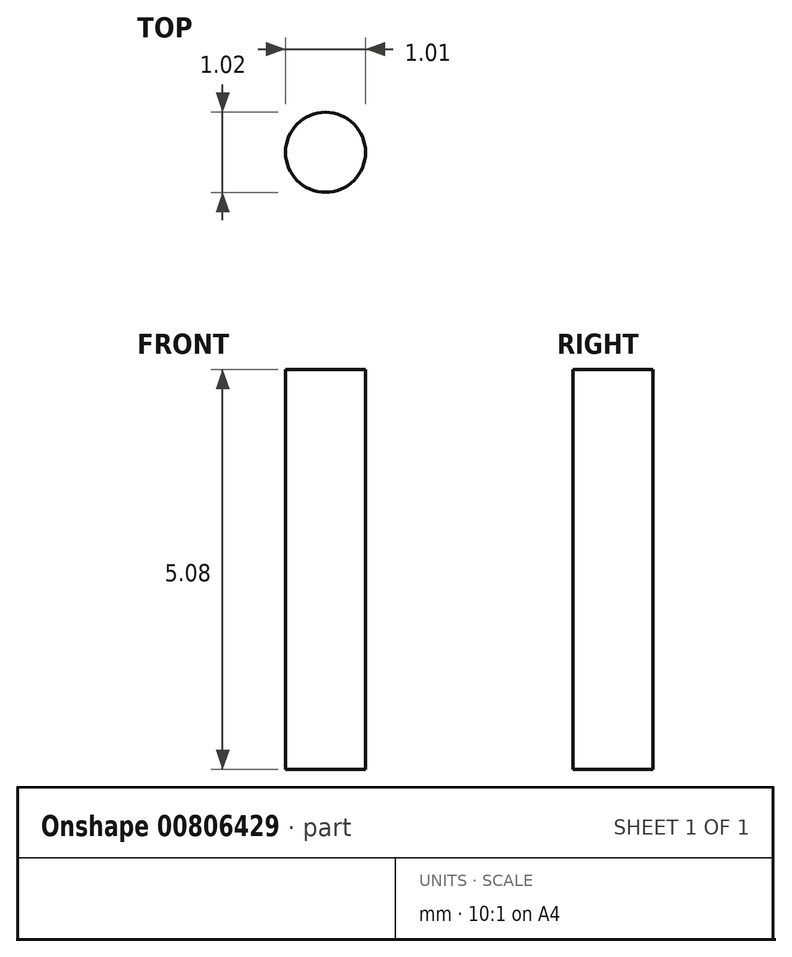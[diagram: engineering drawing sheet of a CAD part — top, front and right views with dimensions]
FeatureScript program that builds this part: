
annotation { "Feature Type Name" : "Feature", "Feature Type Description" : "" }
export const myFeature = defineFeature(function(context is Context, id is Id, definition is map)
    precondition{}
    {
        {
            var Q0;
            Q0=qCreatedBy(makeId("Top.planeOp"),FACE);
            var sketch = newSketch(context, id + "F0", { "sketchPlane" : qUnion([Q0])});
            skCircle(sketch, "E0", {"center": v(56.53, 29.89) * mm, "radius": 0.5 * mm});
            skPoint(sketch, "E0.first.point", {"position": v(56.62, 30.39) * mm});
            skPoint(sketch, "E0.second.point", {"position": v(56.17, 29.52) * mm});
            skPoint(sketch, "E0.third.point", {"position": v(56.84, 29.49) * mm});
            skSolve(sketch);
        }
        {
            var Q0;
            Q0 = qSketchRegion(id + "F0", true);
            extrude(context, id + "F1", {"entities" : qUnion([Q0]), "endBound" : BoundingType.SYMMETRIC, "depth" : 5.08 * mm, "offsetDistance" : 25.4 * mm});
        }
    });
